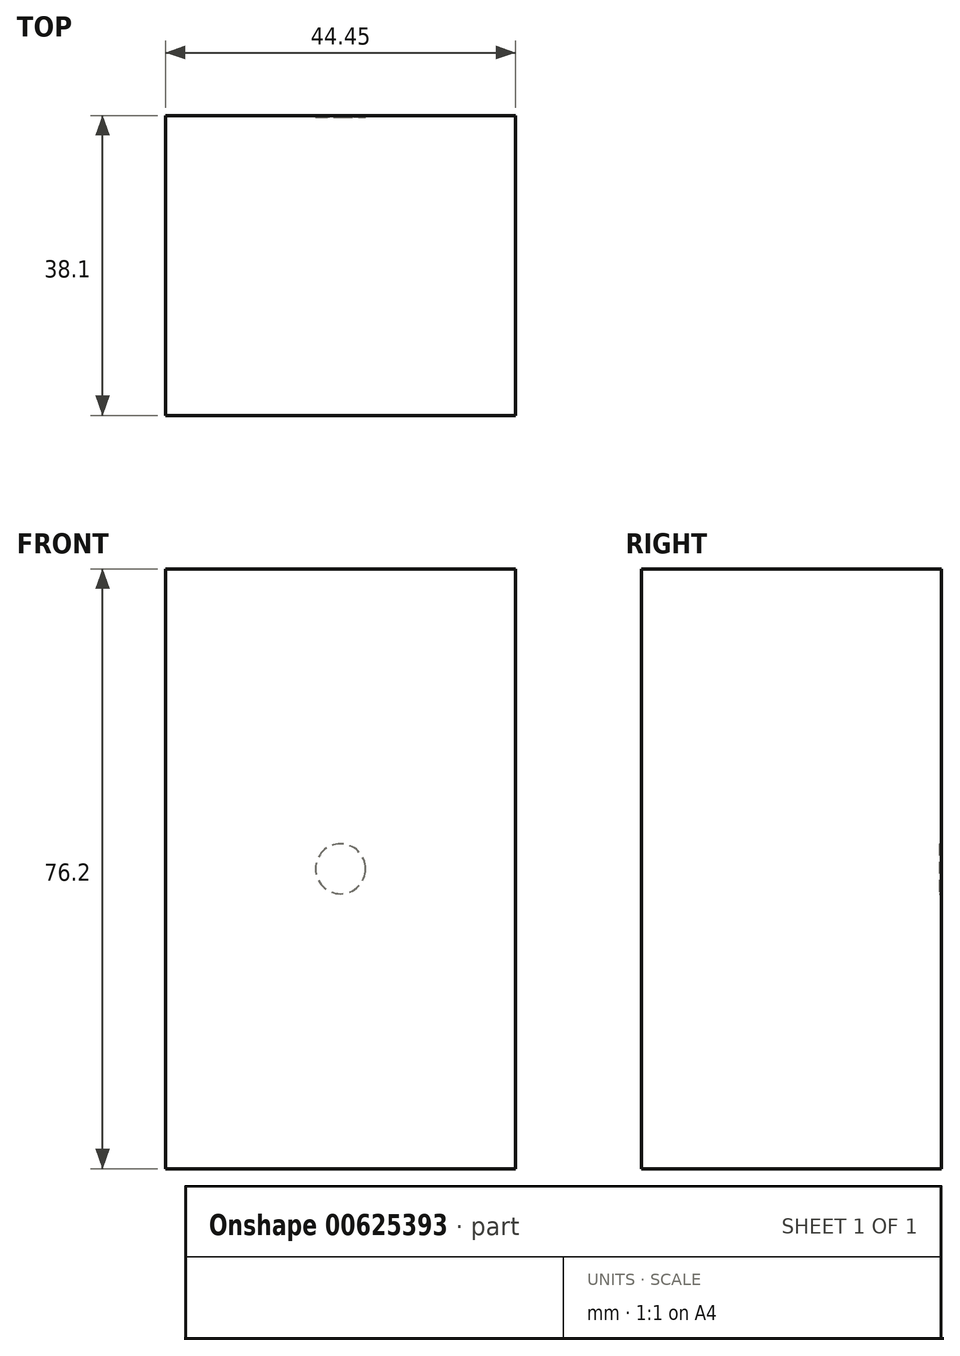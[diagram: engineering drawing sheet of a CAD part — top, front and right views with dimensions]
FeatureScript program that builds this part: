
annotation { "Feature Type Name" : "Feature", "Feature Type Description" : "" }
export const myFeature = defineFeature(function(context is Context, id is Id, definition is map)
    precondition{}
    {
        {
            var Q0;
            Q0=qCreatedBy(makeId("Front.planeOp"),FACE);
            var sketch = newSketch(context, id + "F0", { "sketchPlane" : qUnion([Q0])});
            skLineSegment(sketch, "E0.bottom", {"start": v(0, 0) * mm, "end": v(-44.45, 0) * mm});
            skLineSegment(sketch, "E0.top", {"start": v(0, 76.2) * mm, "end": v(-44.45, 76.2) * mm});
            skLineSegment(sketch, "E0.left", {"start": v(0, 0) * mm, "end": v(0, 76.2) * mm});
            skLineSegment(sketch, "E0.right", {"start": v(-44.45, 0) * mm, "end": v(-44.45, 76.2) * mm});
            skSolve(sketch);
        }
        {
            var Q0;
            Q0=makeQuery(id+"F0.imprint","IMPRINT",FACE,{"disambiguationData":[TD([[makeQuery(id+"F0.imprint","IMPRINT",EDGE,{"derivedFrom":sQuery(id+"F0.wireOp",EDGE,"E0.bottom")}),-1.0]])]});
            extrude(context, id + "F1", {"entities" : qUnion([Q0]), "depth" : 38.1 * mm, "offsetDistance" : 25.4 * mm});
        }
        {
            var Q0;
            Q0=makeQuery(id+"F1.opExtrude","CAP_FACE",FACE,{"disambiguationData":[OSD([sQuery(id+"F0.wireOp",EDGE,"E0.bottom"),sQuery(id+"F0.wireOp",EDGE,"E0.top"),sQuery(id+"F0.wireOp",EDGE,"E0.left"),sQuery(id+"F0.wireOp",EDGE,"E0.right")])],"isStart":true});
            var sketch = newSketch(context, id + "F2", { "sketchPlane" : qUnion([Q0])});
            skLineSegment(sketch, "E1", {"start": v(0, 76.2) * mm, "end": v(44.45, 0) * mm});
            skCircle(sketch, "E2", {"center": v(22.22, 38.1) * mm, "radius": 3.18 * mm});
            skSolve(sketch);
        }
        {
            var Q0;
            {var subQ0=sQuery(id+"F2.wireOp",EDGE,"E2");var subQ1=sQuery(id+"F2.wireOp",EDGE,"E1");var subQ2=makeQuery(id+"F2.imprint","INTERSECT",VERTEX,{"disambiguationData":[OD(0.0)],"derivedFrom":[subQ1,subQ0]});Q0=makeQuery(id+"F2.imprint","IMPRINT",FACE,{"disambiguationData":[TD([[makeQuery(id+"F2.imprint","IMPRINT",EDGE,{"disambiguationData":[TD([[subQ2,-1.0]])],"derivedFrom":subQ1}),1.0]])]});}
            var Q1;
            {var subQ0=sQuery(id+"F2.wireOp",EDGE,"E2");var subQ1=sQuery(id+"F2.wireOp",EDGE,"E1");var subQ2=makeQuery(id+"F2.imprint","INTERSECT",VERTEX,{"disambiguationData":[OD(0.0)],"derivedFrom":[subQ1,subQ0]});Q1=makeQuery(id+"F2.imprint","IMPRINT",FACE,{"disambiguationData":[TD([[makeQuery(id+"F2.imprint","IMPRINT",EDGE,{"disambiguationData":[TD([[subQ2,-1.0]])],"derivedFrom":subQ1}),-1.0]])]});}
            extrude(context, id + "F3", {"entities" : qUnion([Q0, Q1]), "operationType" : NewBodyOperationType.REMOVE, "oppositeDirection" : true, "depth" : 0.23 * mm, "offsetDistance" : 25.4 * mm});
        }
    });
